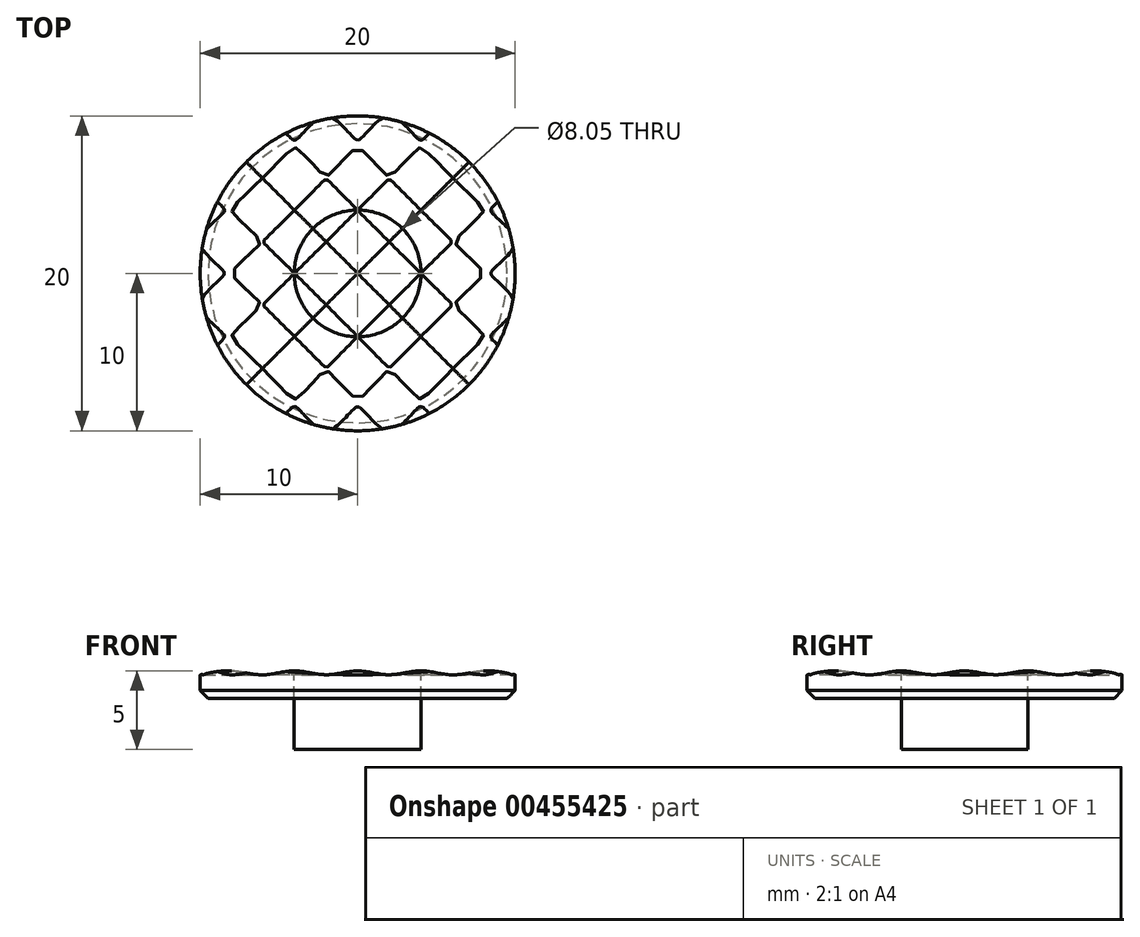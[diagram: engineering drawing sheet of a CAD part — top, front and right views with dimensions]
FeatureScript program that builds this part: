
annotation { "Feature Type Name" : "Feature", "Feature Type Description" : "" }
export const myFeature = defineFeature(function(context is Context, id is Id, definition is map)
    precondition{}
    {
        {
            var Q0;
            Q0=qCreatedBy(makeId("Top.planeOp"),FACE);
            var sketch = newSketch(context, id + "F0", { "sketchPlane" : qUnion([Q0])});
            skCircle(sketch, "E0", {"center": v(0, 0) * mm, "radius": 10 * mm});
            skCircle(sketch, "E1", {"center": v(0, 0) * mm, "radius": 4.03 * mm});
            skSolve(sketch);
        }
        {
            var Q0;
            Q0=makeQuery(id+"F0.imprint","IMPRINT",FACE,{"disambiguationData":[TD([[makeQuery(id+"F0.imprint","IMPRINT",EDGE,{"derivedFrom":sQuery(id+"F0.wireOp",EDGE,"E1")}),1.0]])]});
            extrude(context, id + "F1", {"entities" : qUnion([Q0]), "oppositeDirection" : true, "depth" : 4.75 * mm, "hasSecondDirection" : true, "secondDirectionOppositeDirection" : false, "secondDirectionDepth" : 1 * mm});
        }
        {
            var Q0;
            Q0=makeQuery(id+"F0.imprint","IMPRINT",FACE,{"disambiguationData":[TD([[makeQuery(id+"F0.imprint","IMPRINT",EDGE,{"derivedFrom":sQuery(id+"F0.wireOp",EDGE,"E0")}),1.0]])]});
            extrude(context, id + "F2", {"entities" : qUnion([Q0]), "oppositeDirection" : true, "depth" : 1.5 * mm, "hasSecondDirection" : true, "secondDirectionOppositeDirection" : false, "secondDirectionDepth" : 1 * mm});
        }
        {
            var Q0;
            Q0=qCreatedBy(makeId("Right.planeOp"),FACE);
            var sketch = newSketch(context, id + "F3", { "sketchPlane" : qUnion([Q0])});
            skLineSegment(sketch, "E2", {"start": v(2, 0) * mm, "end": v(2, 3.57) * mm, "construction": true});
            skLineSegment(sketch, "E3", {"start": v(4, 3.57) * mm, "end": v(4, 0) * mm, "construction": true});
            skLineSegment(sketch, "E4", {"start": v(6, 0) * mm, "end": v(6, 3.57) * mm, "construction": true});
            skLineSegment(sketch, "E5", {"start": v(8, 3.57) * mm, "end": v(8, 0) * mm, "construction": true});
            skLineSegment(sketch, "E6", {"start": v(10, 0) * mm, "end": v(10, 3.54) * mm, "construction": true});
            skLineSegment(sketch, "E7", {"start": v(0, 0.25) * mm, "end": v(11.09, 0.25) * mm, "construction": true});
            skLineSegment(sketch, "E8.MirrorCS", {"start": v(0, 0.25) * mm, "end": v(-11.09, 0.25) * mm, "construction": true});
            skLineSegment(sketch, "E9.MirrorCS", {"start": v(-10, 0) * mm, "end": v(-10, 3.54) * mm, "construction": true});
            skLineSegment(sketch, "E10.MirrorCS", {"start": v(-8, 3.57) * mm, "end": v(-8, 0) * mm, "construction": true});
            skLineSegment(sketch, "E11.MirrorCS", {"start": v(-6, 0) * mm, "end": v(-6, 3.57) * mm, "construction": true});
            skLineSegment(sketch, "E12.MirrorCS", {"start": v(-2, 0) * mm, "end": v(-2, 3.57) * mm, "construction": true});
            skLineSegment(sketch, "E13.MirrorCS", {"start": v(-4, 3.57) * mm, "end": v(-4, 0) * mm, "construction": true});
            skLineSegment(sketch, "E14", {"start": v(-10, 0) * mm, "end": v(-10, 1.4) * mm});
            skLineSegment(sketch, "E15", {"start": v(-10, 1.4) * mm, "end": v(10, 1.4) * mm});
            skLineSegment(sketch, "E16", {"start": v(10, 1.4) * mm, "end": v(10, 0) * mm});
            skLineSegment(sketch, "E17", {"start": v(0, 0) * mm, "end": v(0, 3.9) * mm, "construction": true});
            skFitSpline(sketch, "E18", {"points": [v(10, 0) * mm, v(8, 0.25) * mm, v(6, 0) * mm, v(4, 0.25) * mm, v(2, 0) * mm, v(0, 0.25) * mm, v(-2, 0) * mm, v(-4, 0.25) * mm, v(-6, 0) * mm, v(-8, 0.25) * mm, v(-10, 0) * mm], "startDerivative": vector(-20, 4.33) * mm, "endDerivative": vector(-20, -4.33) * mm});
            skSolve(sketch);
        }
        {
            var Q0;
            Q0=makeQuery(id+"F3.imprint","IMPRINT",FACE,{"disambiguationData":[TD([[makeQuery(id+"F3.imprint","IMPRINT",EDGE,{"derivedFrom":sQuery(id+"F3.wireOp",EDGE,"E14")}),-1.0]])]});
            extrude(context, id + "F4", {"entities" : qUnion([Q0]), "operationType" : NewBodyOperationType.REMOVE, "depth" : 12 * mm, "hasSecondDirection" : true, "secondDirectionOppositeDirection" : true, "secondDirectionDepth" : 12 * mm});
        }
        {
            var Q0;
            Q0=makeQuery(id+"F3.imprint","IMPRINT",FACE,{"disambiguationData":[TD([[makeQuery(id+"F3.imprint","IMPRINT",EDGE,{"derivedFrom":sQuery(id+"F3.wireOp",EDGE,"E14")}),-1.0]])]});
            extrude(context, id + "F5", {"entities" : qUnion([Q0]), "oppositeDirection" : true, "depth" : 12 * mm, "hasSecondDirection" : true, "secondDirectionOppositeDirection" : false, "secondDirectionDepth" : 12 * mm});
        }
        {
            var Q0;
            Q0=makeQuery(id+"F5.opExtrude","SWEPT_BODY",BODY,{"disambiguationData":[OSD([sQuery(id+"F3.wireOp",EDGE,"d0056518-e81e-464c-82e9-d38da41b13d6"),sQuery(id+"F3.wireOp",EDGE,"E14"),sQuery(id+"F3.wireOp",EDGE,"E15"),sQuery(id+"F3.wireOp",EDGE,"E16")])]});
            var Q1;
            Q1=sQuery(id+"F3.wireOp",EDGE,"E17");
            transform(context, id + "F6", {"entities" : qUnion([Q0]), "transformType" : TransformType.ROTATION, "transformAxis" : qUnion([Q1]), "angle" : 90 * degree, "makeCopy" : false});
        }
        {
            var Q0;
            Q0=makeQuery(id+"F5.opExtrude","SWEPT_BODY",BODY,{"disambiguationData":[OSD([sQuery(id+"F3.wireOp",EDGE,"d0056518-e81e-464c-82e9-d38da41b13d6"),sQuery(id+"F3.wireOp",EDGE,"E14"),sQuery(id+"F3.wireOp",EDGE,"E15"),sQuery(id+"F3.wireOp",EDGE,"E16")])]});
            var Q1;
            Q1=makeQuery(id+"F2.opExtrude","SWEPT_BODY",BODY,{"disambiguationData":[OSD([sQuery(id+"F0.wireOp",EDGE,"E0"),sQuery(id+"F0.wireOp",EDGE,"E1")])]});
            var Q2;
            Q2=makeQuery(id+"F1.opExtrude","SWEPT_BODY",BODY,{"disambiguationData":[OSD([sQuery(id+"F0.wireOp",EDGE,"E1")])]});
            booleanBodies(context, id + "F7", {"operationType" : BooleanOperationType.SUBTRACTION, "tools" : qUnion([Q0]), "targets" : qUnion([Q1, Q2])});
        }
        {
            var Q0;
            Q0=makeQuery(id+"F2.opExtrude","CAP_EDGE",EDGE,{"disambiguationData":[OSD([sQuery(id+"F0.wireOp",EDGE,"E0")])],"isStart":false});
            chamfer(context, id + "F8", {"entities" : qUnion([Q0]), "width" : .5 * mm, "tangentPropagation" : true});
        }
    });
